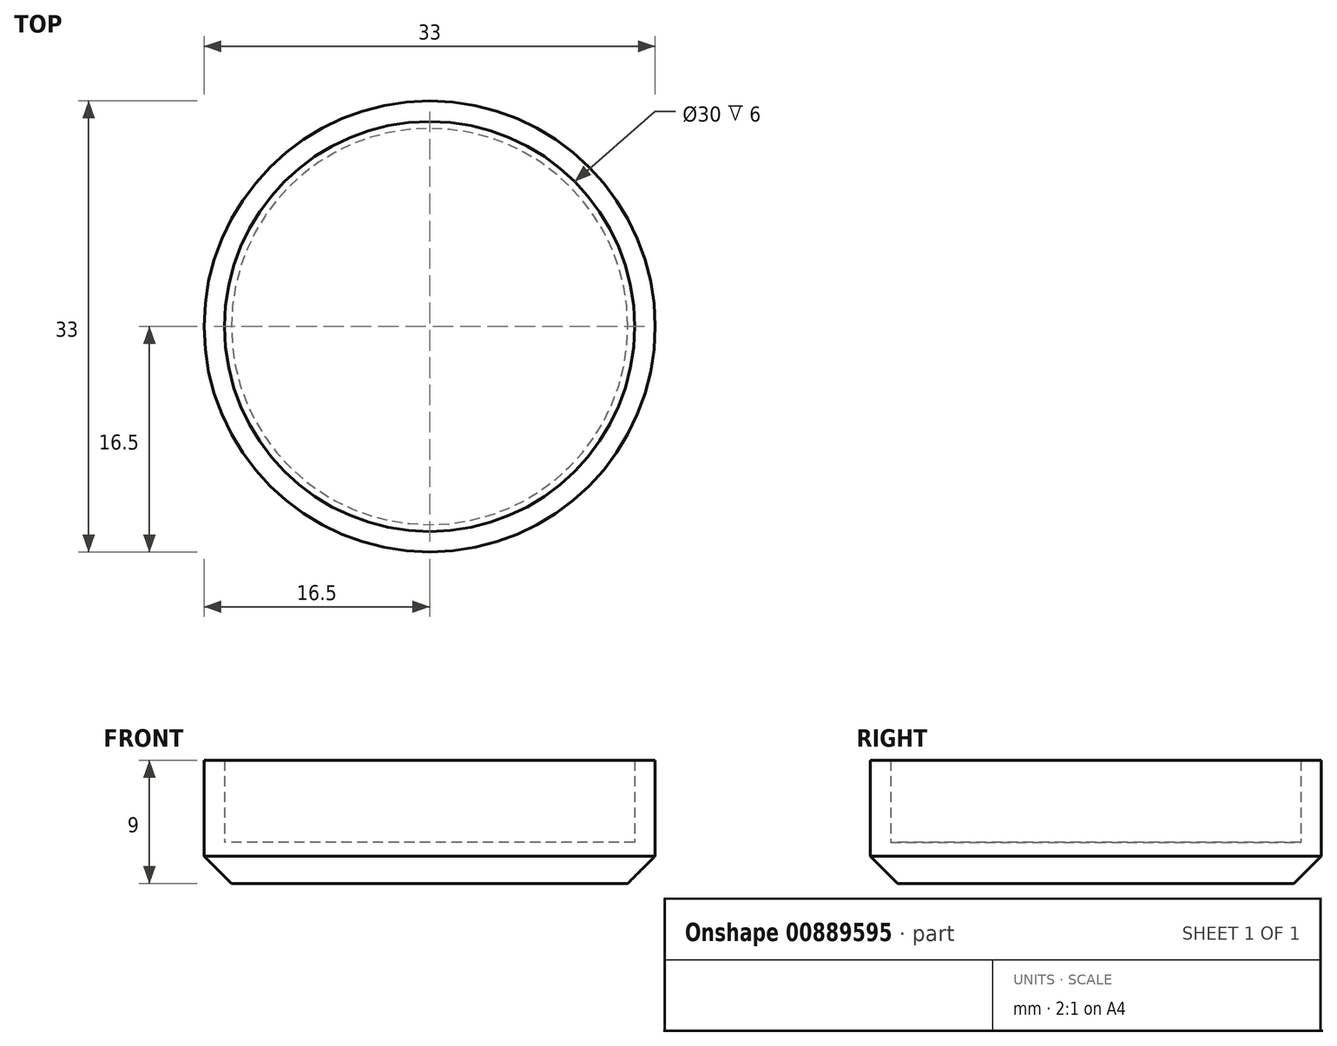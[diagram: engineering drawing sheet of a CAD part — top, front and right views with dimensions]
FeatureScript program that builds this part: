
annotation { "Feature Type Name" : "Feature", "Feature Type Description" : "" }
export const myFeature = defineFeature(function(context is Context, id is Id, definition is map)
    precondition{}
    {
        {
            var Q0;
            Q0=qCreatedBy(makeId("Top.planeOp"),FACE);
            var sketch = newSketch(context, id + "F0", { "sketchPlane" : qUnion([Q0])});
            skCircle(sketch, "E0", {"center": v(0, 0) * mm, "radius": 16.5 * mm});
            skSolve(sketch);
        }
        {
            var Q0;
            Q0=makeQuery(id+"F0.imprint","IMPRINT",FACE,{"disambiguationData":[TD([[makeQuery(id+"F0.imprint","IMPRINT",EDGE,{"derivedFrom":sQuery(id+"F0.wireOp",EDGE,"E0")}),1.0]])]});
            extrude(context, id + "F1", {"entities" : qUnion([Q0]), "depth" : 3 * mm, "offsetDistance" : 25 * mm});
        }
        {
            var Q0;
            Q0=makeQuery(id+"F1.opExtrude","CAP_FACE",FACE,{"disambiguationData":[OSD([sQuery(id+"F0.wireOp",EDGE,"E0")])],"isStart":false});
            var sketch = newSketch(context, id + "F2", { "sketchPlane" : qUnion([Q0])});
            skCircle(sketch, "E1", {"center": v(0, 0) * mm, "radius": 16.5 * mm});
            skCircle(sketch, "E2", {"center": v(0, 0) * mm, "radius": 15 * mm});
            skSolve(sketch);
        }
        {
            var Q0;
            Q0=makeQuery(id+"F2.imprint","IMPRINT",FACE,{"disambiguationData":[TD([[makeQuery(id+"F2.imprint","IMPRINT",EDGE,{"derivedFrom":sQuery(id+"F2.wireOp",EDGE,"E1")}),1.0]])]});
            extrude(context, id + "F3", {"entities" : qUnion([Q0]), "operationType" : NewBodyOperationType.ADD, "depth" : 6 * mm, "offsetDistance" : 25 * mm});
        }
        {
            var Q0;
            Q0=makeQuery(id+"F1.opExtrude","CAP_EDGE",EDGE,{"disambiguationData":[OSD([sQuery(id+"F0.wireOp",EDGE,"E0")])],"isStart":true});
            chamfer(context, id + "F4", {"entities" : qUnion([Q0]), "width" : 2 * mm, "tangentPropagation" : true});
        }
    });
